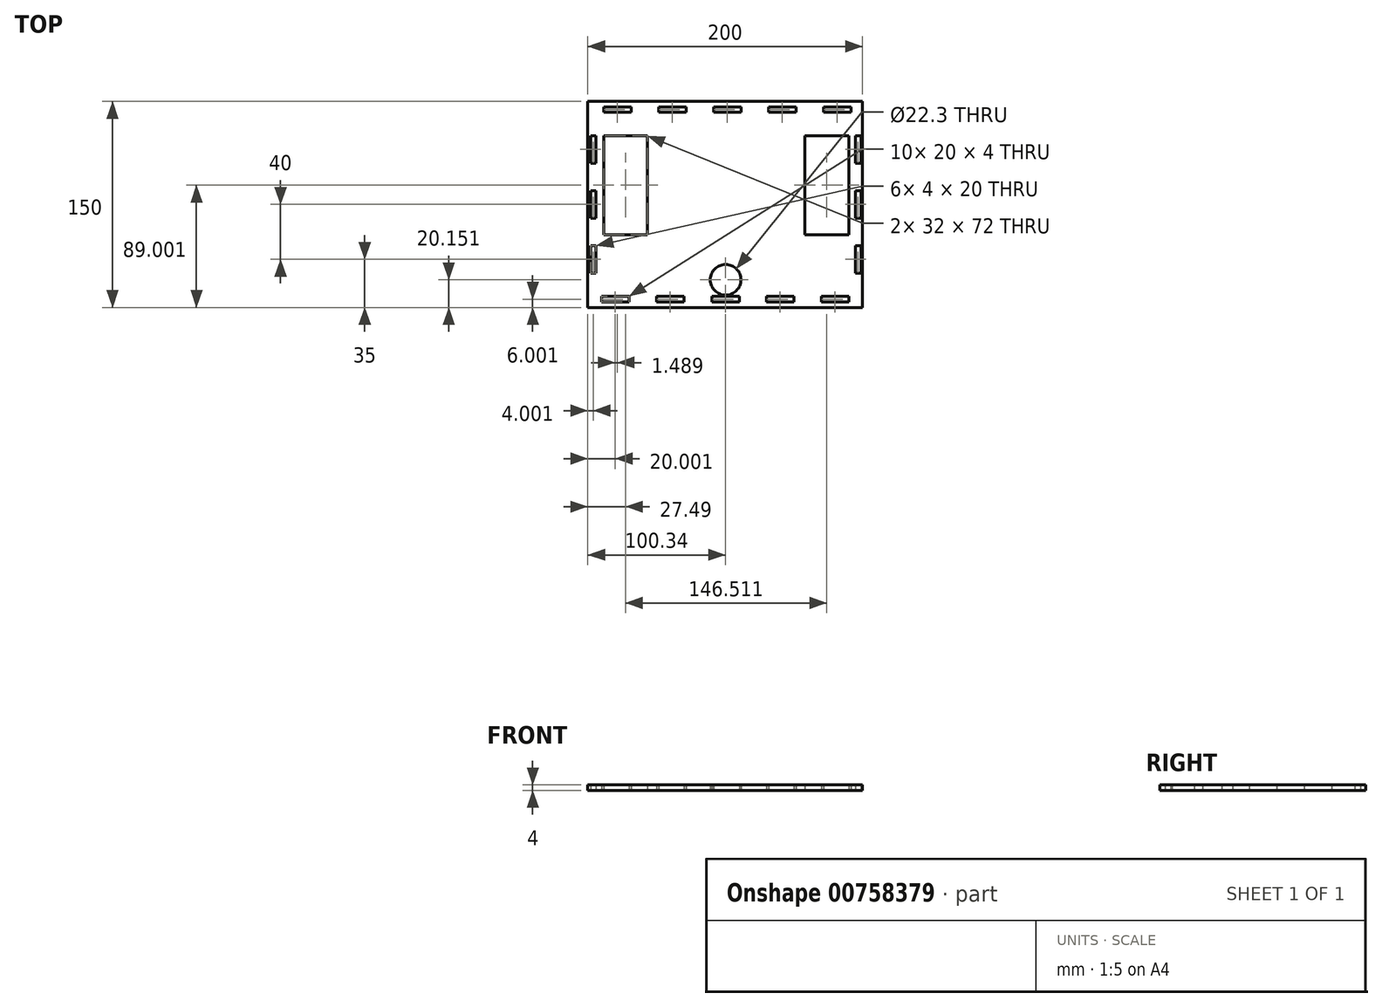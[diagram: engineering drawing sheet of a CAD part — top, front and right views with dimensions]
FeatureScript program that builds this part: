
annotation { "Feature Type Name" : "Feature", "Feature Type Description" : "" }
export const myFeature = defineFeature(function(context is Context, id is Id, definition is map)
    precondition{}
    {
        {
            var Q0;
            Q0=qCreatedBy(makeId("Top.planeOp"),FACE);
            var sketch = newSketch(context, id + "F0", { "sketchPlane" : qUnion([Q0])});
            skLineSegment(sketch, "E0.bottom", {"start": v(99.66, 75.42) * mm, "end": v(-100.34, 75.42) * mm});
            skLineSegment(sketch, "E0.top", {"start": v(99.66, -74.58) * mm, "end": v(-100.34, -74.58) * mm});
            skLineSegment(sketch, "E0.left", {"start": v(99.66, 75.42) * mm, "end": v(99.66, -74.58) * mm});
            skLineSegment(sketch, "E0.right", {"start": v(-100.34, 75.42) * mm, "end": v(-100.34, -74.58) * mm});
            skPoint(sketch, "E0.middle", {"position": v(-0.34, 0.42) * mm});
            skPoint(sketch, "E1", {"position": v(-0.34, 75.42) * mm});
            skPoint(sketch, "E2", {"position": v(99.66, 0.42) * mm});
            skLineSegment(sketch, "E3", {"start": v(9.66, 75.42) * mm, "end": v(29.66, 75.42) * mm});
            skLineSegment(sketch, "E4", {"start": v(99.66, -9.58) * mm, "end": v(99.66, -29.58) * mm});
            skLineSegment(sketch, "E5", {"start": v(99.66, -49.58) * mm, "end": v(99.66, -69.58) * mm});
            skLineSegment(sketch, "E6.bottom", {"start": v(-88.85, 50.42) * mm, "end": v(-56.85, 50.42) * mm});
            skLineSegment(sketch, "E6.top", {"start": v(-88.85, -21.58) * mm, "end": v(-56.85, -21.58) * mm});
            skLineSegment(sketch, "E6.left", {"start": v(-88.85, 50.42) * mm, "end": v(-88.85, -21.58) * mm});
            skLineSegment(sketch, "E6.right", {"start": v(-56.85, 50.42) * mm, "end": v(-56.85, -21.58) * mm});
            skLineSegment(sketch, "E7.MirrorCS", {"start": v(57.66, 50.42) * mm, "end": v(57.66, -21.58) * mm});
            skLineSegment(sketch, "E8.MirrorCS", {"start": v(89.66, 50.42) * mm, "end": v(57.66, 50.42) * mm});
            skLineSegment(sketch, "E9.MirrorCS", {"start": v(89.66, 50.42) * mm, "end": v(89.66, -21.58) * mm});
            skLineSegment(sketch, "E10.MirrorCS", {"start": v(89.66, -21.58) * mm, "end": v(57.66, -21.58) * mm});
            skLineSegment(sketch, "E11.bottom", {"start": v(-88.85, 71.42) * mm, "end": v(-68.85, 71.42) * mm});
            skLineSegment(sketch, "E11.top", {"start": v(-88.85, 67.42) * mm, "end": v(-68.85, 67.42) * mm});
            skLineSegment(sketch, "E11.left", {"start": v(-88.85, 71.42) * mm, "end": v(-88.85, 67.42) * mm});
            skLineSegment(sketch, "E11.right", {"start": v(-68.85, 71.42) * mm, "end": v(-68.85, 67.42) * mm});
            skLineSegment(sketch, "E12.1.0.0", {"start": v(-48.85, 71.42) * mm, "end": v(-28.85, 71.42) * mm});
            skLineSegment(sketch, "E12.1.0.1", {"start": v(-48.85, 67.42) * mm, "end": v(-28.85, 67.42) * mm});
            skLineSegment(sketch, "E12.1.0.2", {"start": v(-28.85, 71.42) * mm, "end": v(-28.85, 67.42) * mm});
            skLineSegment(sketch, "E12.1.0.3", {"start": v(-48.85, 71.42) * mm, "end": v(-48.85, 67.42) * mm});
            skLineSegment(sketch, "E12.2.0.0", {"start": v(-8.85, 71.42) * mm, "end": v(11.15, 71.42) * mm});
            skLineSegment(sketch, "E12.2.0.1", {"start": v(-8.85, 67.42) * mm, "end": v(11.15, 67.42) * mm});
            skLineSegment(sketch, "E12.2.0.2", {"start": v(11.15, 71.42) * mm, "end": v(11.15, 67.42) * mm});
            skLineSegment(sketch, "E12.2.0.3", {"start": v(-8.85, 71.42) * mm, "end": v(-8.85, 67.42) * mm});
            skLineSegment(sketch, "E12.3.0.0", {"start": v(31.15, 71.42) * mm, "end": v(51.15, 71.42) * mm});
            skLineSegment(sketch, "E12.3.0.1", {"start": v(31.15, 67.42) * mm, "end": v(51.15, 67.42) * mm});
            skLineSegment(sketch, "E12.3.0.2", {"start": v(51.15, 71.42) * mm, "end": v(51.15, 67.42) * mm});
            skLineSegment(sketch, "E12.3.0.3", {"start": v(31.15, 71.42) * mm, "end": v(31.15, 67.42) * mm});
            skLineSegment(sketch, "E12.4.0.0", {"start": v(71.15, 71.42) * mm, "end": v(91.15, 71.42) * mm});
            skLineSegment(sketch, "E12.4.0.1", {"start": v(71.15, 67.42) * mm, "end": v(91.15, 67.42) * mm});
            skLineSegment(sketch, "E12.4.0.2", {"start": v(91.15, 71.42) * mm, "end": v(91.15, 67.42) * mm});
            skLineSegment(sketch, "E12.4.0.3", {"start": v(71.15, 71.42) * mm, "end": v(71.15, 67.42) * mm});
            skLineSegment(sketch, "E12.direction1", {"start": v(-88.85, 71.42) * mm, "end": v(-48.85, 71.42) * mm, "construction": true});
            skPoint(sketch, "E13", {"position": v(-100.34, 0.42) * mm});
            skLineSegment(sketch, "E14", {"start": v(-98.34, 0.42) * mm, "end": v(-98.34, 10.42) * mm});
            skLineSegment(sketch, "E15", {"start": v(-98.34, 0.42) * mm, "end": v(-98.34, -9.58) * mm});
            skLineSegment(sketch, "E16", {"start": v(-98.34, -9.58) * mm, "end": v(-94.34, -9.58) * mm});
            skLineSegment(sketch, "E17", {"start": v(-94.34, 10.42) * mm, "end": v(-98.34, 10.42) * mm});
            skLineSegment(sketch, "E18", {"start": v(-94.34, 0.42) * mm, "end": v(-94.34, 10.42) * mm});
            skLineSegment(sketch, "E19", {"start": v(-94.34, -9.58) * mm, "end": v(-94.34, 0.42) * mm});
            skLineSegment(sketch, "E20.0.1.0", {"start": v(-98.34, 40.42) * mm, "end": v(-98.34, 50.42) * mm});
            skLineSegment(sketch, "E20.0.1.1", {"start": v(-94.34, 40.42) * mm, "end": v(-94.34, 50.42) * mm});
            skLineSegment(sketch, "E20.0.1.2", {"start": v(-94.34, 50.42) * mm, "end": v(-98.34, 50.42) * mm});
            skLineSegment(sketch, "E20.0.1.3", {"start": v(-98.34, 40.42) * mm, "end": v(-98.34, 30.42) * mm});
            skLineSegment(sketch, "E20.0.1.4", {"start": v(-98.34, 30.42) * mm, "end": v(-94.34, 30.42) * mm});
            skLineSegment(sketch, "E20.0.1.5", {"start": v(-94.34, 30.42) * mm, "end": v(-94.34, 40.42) * mm});
            skLineSegment(sketch, "E20.direction1", {"start": v(-98.34, 0.42) * mm, "end": v(-73.34, 0.42) * mm, "construction": true});
            skLineSegment(sketch, "E21.MirrorCS", {"start": v(-94.34, 0.42) * mm, "end": v(-94.34, -9.58) * mm});
            skLineSegment(sketch, "E22.MirrorCS", {"start": v(-94.34, -29.58) * mm, "end": v(-94.34, -39.58) * mm});
            skLineSegment(sketch, "E23.MirrorCS", {"start": v(-98.34, -29.58) * mm, "end": v(-94.34, -29.58) * mm});
            skLineSegment(sketch, "E24.MirrorCS", {"start": v(-98.34, -39.58) * mm, "end": v(-98.34, -49.58) * mm});
            skLineSegment(sketch, "E25.MirrorCS", {"start": v(-94.34, -39.58) * mm, "end": v(-94.34, -49.58) * mm});
            skLineSegment(sketch, "E26", {"start": v(-98.34, -39.58) * mm, "end": v(-98.34, -29.58) * mm});
            skLineSegment(sketch, "E27", {"start": v(-98.34, -49.58) * mm, "end": v(-94.34, -49.58) * mm});
            skLineSegment(sketch, "E28.MirrorCS", {"start": v(94.52, 0.42) * mm, "end": v(94.52, -9.58) * mm});
            skLineSegment(sketch, "E29.MirrorCS", {"start": v(98.52, 0.42) * mm, "end": v(98.52, -9.58) * mm});
            skLineSegment(sketch, "E30.MirrorCS", {"start": v(98.52, 0.42) * mm, "end": v(98.52, 10.42) * mm});
            skLineSegment(sketch, "E31.MirrorCS", {"start": v(94.52, 0.42) * mm, "end": v(94.52, 10.42) * mm});
            skLineSegment(sketch, "E32.MirrorCS", {"start": v(94.52, 10.42) * mm, "end": v(98.52, 10.42) * mm});
            skLineSegment(sketch, "E33.MirrorCS", {"start": v(98.52, -9.58) * mm, "end": v(94.52, -9.58) * mm});
            skLineSegment(sketch, "E34.MirrorCS", {"start": v(94.52, -29.58) * mm, "end": v(94.52, -39.58) * mm});
            skLineSegment(sketch, "E35.MirrorCS", {"start": v(94.52, -39.58) * mm, "end": v(94.52, -49.58) * mm});
            skLineSegment(sketch, "E36.MirrorCS", {"start": v(98.52, -39.58) * mm, "end": v(98.52, -49.58) * mm});
            skLineSegment(sketch, "E37.MirrorCS", {"start": v(98.52, -39.58) * mm, "end": v(98.52, -29.58) * mm});
            skLineSegment(sketch, "E38.MirrorCS", {"start": v(98.52, -29.58) * mm, "end": v(94.52, -29.58) * mm});
            skLineSegment(sketch, "E39.MirrorCS", {"start": v(98.52, -49.58) * mm, "end": v(94.52, -49.58) * mm});
            skLineSegment(sketch, "E40.MirrorCS", {"start": v(98.52, 30.42) * mm, "end": v(94.52, 30.42) * mm});
            skLineSegment(sketch, "E41.MirrorCS", {"start": v(98.52, 40.42) * mm, "end": v(98.52, 30.42) * mm});
            skLineSegment(sketch, "E42.MirrorCS", {"start": v(94.52, 30.42) * mm, "end": v(94.52, 40.42) * mm});
            skLineSegment(sketch, "E43.MirrorCS", {"start": v(98.52, 40.42) * mm, "end": v(98.52, 50.42) * mm});
            skLineSegment(sketch, "E44.MirrorCS", {"start": v(94.52, 40.42) * mm, "end": v(94.52, 50.42) * mm});
            skLineSegment(sketch, "E45.MirrorCS", {"start": v(94.52, 50.42) * mm, "end": v(98.52, 50.42) * mm});
            skLineSegment(sketch, "E46.MirrorCS", {"start": v(29.66, -70.58) * mm, "end": v(29.66, -66.58) * mm});
            skLineSegment(sketch, "E47.MirrorCS", {"start": v(49.66, -70.58) * mm, "end": v(49.66, -66.58) * mm});
            skLineSegment(sketch, "E48.MirrorCS", {"start": v(29.66, -70.58) * mm, "end": v(49.66, -70.58) * mm});
            skLineSegment(sketch, "E49.MirrorCS", {"start": v(29.66, -66.58) * mm, "end": v(49.66, -66.58) * mm});
            skLineSegment(sketch, "E50.MirrorCS", {"start": v(69.66, -70.58) * mm, "end": v(69.66, -66.58) * mm});
            skLineSegment(sketch, "E51.MirrorCS", {"start": v(69.66, -70.58) * mm, "end": v(89.66, -70.58) * mm});
            skLineSegment(sketch, "E52.MirrorCS", {"start": v(69.66, -66.58) * mm, "end": v(89.66, -66.58) * mm});
            skLineSegment(sketch, "E53.MirrorCS", {"start": v(89.66, -70.58) * mm, "end": v(89.66, -66.58) * mm});
            skLineSegment(sketch, "E54.MirrorCS", {"start": v(-90.34, -66.58) * mm, "end": v(-70.34, -66.58) * mm});
            skLineSegment(sketch, "E55.MirrorCS", {"start": v(-90.34, -70.58) * mm, "end": v(-90.34, -66.58) * mm});
            skLineSegment(sketch, "E56.MirrorCS", {"start": v(-70.34, -70.58) * mm, "end": v(-70.34, -66.58) * mm});
            skLineSegment(sketch, "E57.MirrorCS", {"start": v(-50.34, -70.58) * mm, "end": v(-50.34, -66.58) * mm});
            skLineSegment(sketch, "E58.MirrorCS", {"start": v(-30.34, -70.58) * mm, "end": v(-30.34, -66.58) * mm});
            skLineSegment(sketch, "E59.MirrorCS", {"start": v(-50.34, -70.58) * mm, "end": v(-30.34, -70.58) * mm});
            skLineSegment(sketch, "E60", {"start": v(-90.34, -70.58) * mm, "end": v(-70.34, -70.58) * mm});
            skPoint(sketch, "E61", {"position": v(0, -54.43) * mm});
            skCircle(sketch, "E62", {"center": v(0, -54.43) * mm, "radius": 11.15 * mm});
            skLineSegment(sketch, "E63", {"start": v(0, -66.58) * mm, "end": v(10, -66.58) * mm});
            skLineSegment(sketch, "E64", {"start": v(0, -66.58) * mm, "end": v(-10, -66.58) * mm});
            skLineSegment(sketch, "E65", {"start": v(-10, -66.58) * mm, "end": v(-10, -70.58) * mm});
            skLineSegment(sketch, "E66", {"start": v(-10, -70.58) * mm, "end": v(10, -70.58) * mm});
            skLineSegment(sketch, "E67", {"start": v(10, -70.58) * mm, "end": v(10, -66.58) * mm});
            skLineSegment(sketch, "E68", {"start": v(-50.34, -66.58) * mm, "end": v(-30.34, -66.58) * mm});
            skSolve(sketch);
        }
        {
            var Q0;
            {var subQ5=sQuery(id+"F0.wireOp",EDGE,"E0.top");Q0=makeQuery(id+"F0.imprint","IMPRINT",FACE,{"disambiguationData":[TD([[makeQuery(id+"F0.imprint","IMPRINT",EDGE,{"derivedFrom":subQ5}),-1.0]])]});}
            extrude(context, id + "F1", {"entities" : qUnion([Q0]), "depth" : 4 * mm});
        }
    });
